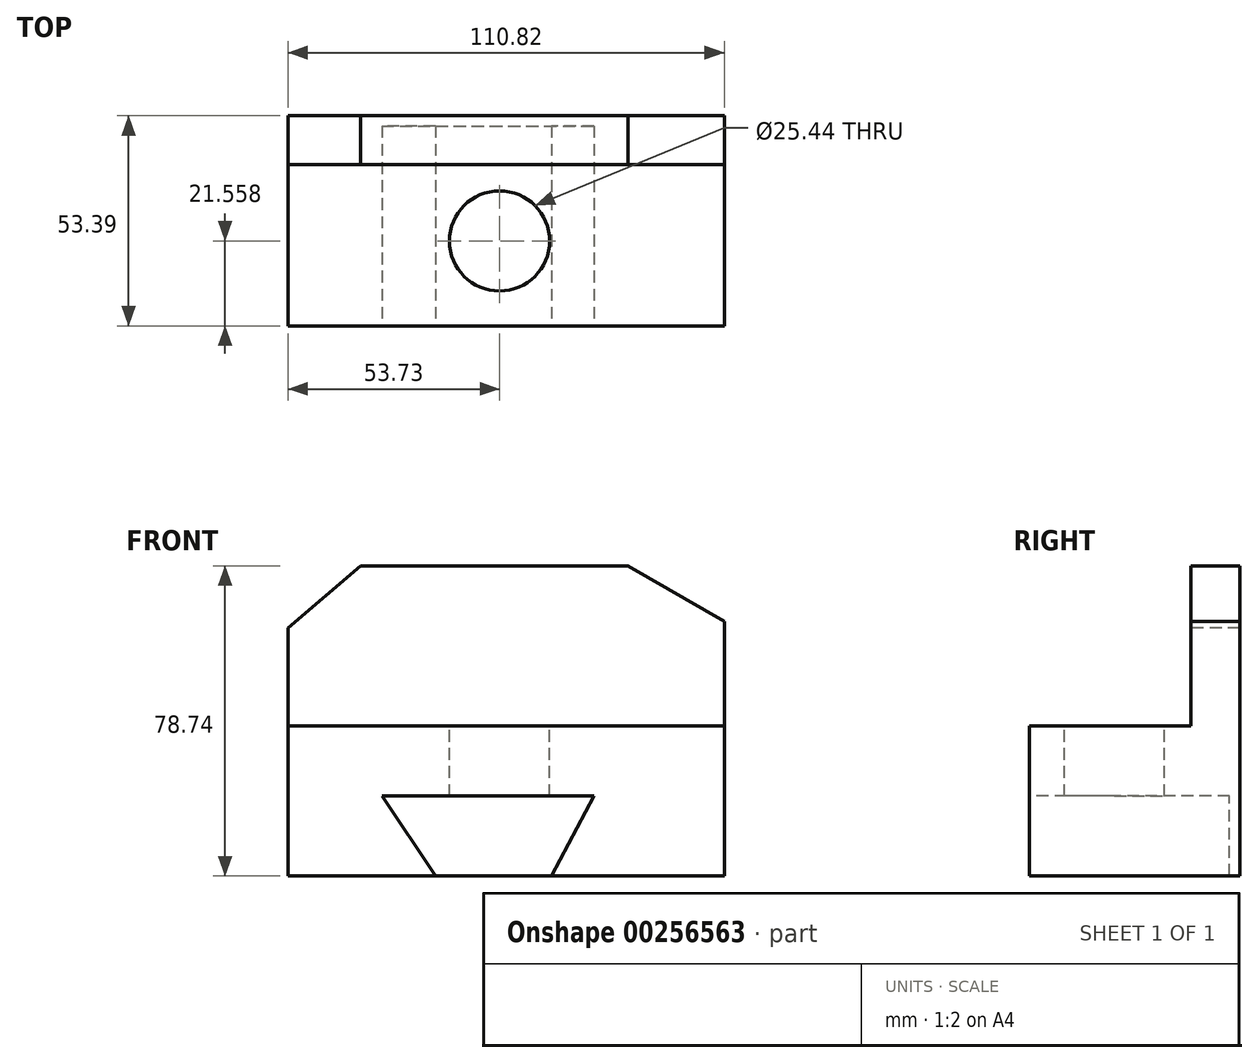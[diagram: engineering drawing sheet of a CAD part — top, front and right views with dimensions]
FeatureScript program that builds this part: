
annotation { "Feature Type Name" : "Feature", "Feature Type Description" : "" }
export const myFeature = defineFeature(function(context is Context, id is Id, definition is map)
    precondition{}
    {
        {
            var Q0;
            Q0=qCreatedBy(makeId("Top.planeOp"),FACE);
            var sketch = newSketch(context, id + "F0", { "sketchPlane" : qUnion([Q0])});
            skLineSegment(sketch, "E0.bottom", {"start": v(-53.73, 14.52) * mm, "end": v(57.1, 14.52) * mm});
            skLineSegment(sketch, "E0.top", {"start": v(-53.73, -38.87) * mm, "end": v(57.1, -38.87) * mm});
            skLineSegment(sketch, "E0.left", {"start": v(-53.73, 14.52) * mm, "end": v(-53.73, -38.87) * mm});
            skLineSegment(sketch, "E0.right", {"start": v(57.1, 14.52) * mm, "end": v(57.1, -38.87) * mm});
            skSolve(sketch);
        }
        {
            var Q0;
            Q0=makeQuery(id+"F0.imprint","IMPRINT",FACE,{"disambiguationData":[TD([[makeQuery(id+"F0.imprint","IMPRINT",EDGE,{"derivedFrom":sQuery(id+"F0.wireOp",EDGE,"E0.bottom")}),-1.0]])]});
            extrude(context, id + "F1", {"entities" : qUnion([Q0]), "depth" : 38.1 * mm});
        }
        {
            var Q0;
            Q0=makeQuery(id+"F1.opExtrude","CAP_FACE",FACE,{"disambiguationData":[OSD([sQuery(id+"F0.wireOp",EDGE,"E0.bottom"),sQuery(id+"F0.wireOp",EDGE,"E0.top"),sQuery(id+"F0.wireOp",EDGE,"E0.left"),sQuery(id+"F0.wireOp",EDGE,"E0.right")])],"isStart":false});
            var sketch = newSketch(context, id + "F2", { "sketchPlane" : qUnion([Q0])});
            skLineSegment(sketch, "E1.bottom", {"start": v(-53.73, 14.52) * mm, "end": v(57.1, 14.52) * mm});
            skLineSegment(sketch, "E1.top", {"start": v(-53.73, 2.1) * mm, "end": v(57.1, 2.1) * mm});
            skLineSegment(sketch, "E1.left", {"start": v(-53.73, 14.52) * mm, "end": v(-53.73, 2.1) * mm});
            skLineSegment(sketch, "E1.right", {"start": v(57.1, 14.52) * mm, "end": v(57.1, 2.1) * mm});
            skSolve(sketch);
        }
        {
            var Q0;
            Q0=makeQuery(id+"F2.imprint","IMPRINT",FACE,{"disambiguationData":[TD([[makeQuery(id+"F2.imprint","IMPRINT",EDGE,{"derivedFrom":sQuery(id+"F2.wireOp",EDGE,"E1.bottom")}),-1.0]])]});
            extrude(context, id + "F3", {"entities" : qUnion([Q0]), "operationType" : NewBodyOperationType.ADD, "depth" : 40.64 * mm});
        }
        {
            var Q0;
            Q0=makeQuery(id+"F3.opExtrude","SWEPT_FACE",FACE,{"disambiguationData":[OSD([sQuery(id+"F2.wireOp",EDGE,"E1.top")])]});
            var sketch = newSketch(context, id + "F4", { "sketchPlane" : qUnion([Q0])});
            skLineSegment(sketch, "E2", {"start": v(-35.27, 78.74) * mm, "end": v(-53.73, 63) * mm});
            skLineSegment(sketch, "E3", {"start": v(32.62, 78.74) * mm, "end": v(57.1, 64.6) * mm});
            skSolve(sketch);
        }
        {
            var Q0;
            {var subQ0=sQuery(id+"F4.wireOp",EDGE,"E2");Q0=makeQuery(id+"F4.imprint","IMPRINT",FACE,{"disambiguationData":[TD([[makeQuery(id+"F4.imprint","IMPRINT",EDGE,{"derivedFrom":subQ0}),-1.0]])]});}
            var Q1;
            {var subQ0=sQuery(id+"F4.wireOp",EDGE,"E3");Q1=makeQuery(id+"F4.imprint","IMPRINT",FACE,{"disambiguationData":[TD([[makeQuery(id+"F4.imprint","IMPRINT",EDGE,{"derivedFrom":subQ0}),1.0]])]});}
            extrude(context, id + "F5", {"entities" : qUnion([Q0, Q1]), "operationType" : NewBodyOperationType.REMOVE, "oppositeDirection" : true, "depth" : 25.4 * mm});
        }
        {
            var Q0;
            Q0=makeQuery(id+"F1.opExtrude","SWEPT_FACE",FACE,{"disambiguationData":[OSD([sQuery(id+"F0.wireOp",EDGE,"E0.top")])]});
            var sketch = newSketch(context, id + "F6", { "sketchPlane" : qUnion([Q0])});
            skLineSegment(sketch, "E4", {"start": v(-16.3, 0) * mm, "end": v(-29.88, 20.26) * mm});
            skLineSegment(sketch, "E5", {"start": v(-29.88, 20.26) * mm, "end": v(24.03, 20.26) * mm});
            skLineSegment(sketch, "E6", {"start": v(24.03, 20.26) * mm, "end": v(13.25, 0) * mm});
            skSolve(sketch);
        }
        {
            var Q0;
            {var subQ0=sQuery(id+"F6.wireOp",EDGE,"E4");Q0=makeQuery(id+"F6.imprint","IMPRINT",FACE,{"disambiguationData":[TD([[makeQuery(id+"F6.imprint","IMPRINT",EDGE,{"derivedFrom":subQ0}),-1.0]])]});}
            extrude(context, id + "F7", {"entities" : qUnion([Q0]), "operationType" : NewBodyOperationType.REMOVE, "oppositeDirection" : true, "depth" : 25.4 * mm});
        }
        {
            var Q0;
            Q0=makeQuery(id+"F7.boolean.opBoolean","COPY",FACE,{"derivedFrom":makeQuery(id+"F7.opExtrude","CAP_FACE",FACE,{"disambiguationData":[OSD([sQuery(id+"F0.wireOp",EDGE,"E0.top"),sQuery(id+"F6.wireOp",EDGE,"E4"),sQuery(id+"F6.wireOp",EDGE,"E5"),sQuery(id+"F6.wireOp",EDGE,"E6")])],"isStart":false})});
            extrude(context, id + "F8", {"entities" : qUnion([Q0]), "operationType" : NewBodyOperationType.REMOVE, "oppositeDirection" : true, "depth" : 25.4 * mm});
        }
        {
            var Q0;
            Q0=makeQuery(id+"F1.opExtrude","CAP_FACE",FACE,{"disambiguationData":[OSD([sQuery(id+"F0.wireOp",EDGE,"E0.bottom"),sQuery(id+"F0.wireOp",EDGE,"E0.top"),sQuery(id+"F0.wireOp",EDGE,"E0.left"),sQuery(id+"F0.wireOp",EDGE,"E0.right")])],"isStart":false});
            var sketch = newSketch(context, id + "F9", { "sketchPlane" : qUnion([Q0])});
            skLineSegment(sketch, "E7", {"start": v(0, -17.31) * mm, "end": v(0, -38.87) * mm});
            skLineSegment(sketch, "E8", {"start": v(0, -17.31) * mm, "end": v(-15.5, -17.31) * mm});
            skLineSegment(sketch, "E9", {"start": v(0, -17.31) * mm, "end": v(15.05, -17.31) * mm});
            skLineSegment(sketch, "E10", {"start": v(0, -17.31) * mm, "end": v(0, 0) * mm});
            skCircle(sketch, "E11", {"center": v(0, -17.31) * mm, "radius": 12.72 * mm});
            skSolve(sketch);
        }
        {
            var Q0;
            {var subQ1=sQuery(id+"F9.wireOp",EDGE,"E8");var subQ3=sQuery(id+"F9.wireOp",EDGE,"E11");var subQ4=makeQuery(id+"F9.imprint","INTERSECT",VERTEX,{"derivedFrom":[subQ1,subQ3]});Q0=makeQuery(id+"F9.imprint","IMPRINT",FACE,{"disambiguationData":[TD([[makeQuery(id+"F9.imprint","IMPRINT",EDGE,{"disambiguationData":[TD([[subQ4,1.0]])],"derivedFrom":subQ3}),1.0]])]});}
            var Q1;
            {var subQ1=sQuery(id+"F9.wireOp",EDGE,"E9");var subQ3=sQuery(id+"F9.wireOp",EDGE,"E11");var subQ4=makeQuery(id+"F9.imprint","INTERSECT",VERTEX,{"derivedFrom":[subQ1,subQ3]});Q1=makeQuery(id+"F9.imprint","IMPRINT",FACE,{"disambiguationData":[TD([[makeQuery(id+"F9.imprint","IMPRINT",EDGE,{"disambiguationData":[TD([[subQ4,-1.0]])],"derivedFrom":subQ3}),1.0]])]});}
            var Q2;
            {var subQ1=sQuery(id+"F9.wireOp",EDGE,"E7");var subQ3=sQuery(id+"F9.wireOp",EDGE,"E11");var subQ4=makeQuery(id+"F9.imprint","INTERSECT",VERTEX,{"derivedFrom":[subQ1,subQ3]});Q2=makeQuery(id+"F9.imprint","IMPRINT",FACE,{"disambiguationData":[TD([[makeQuery(id+"F9.imprint","IMPRINT",EDGE,{"disambiguationData":[TD([[subQ4,1.0]])],"derivedFrom":subQ3}),1.0]])]});}
            var Q3;
            {var subQ1=sQuery(id+"F9.wireOp",EDGE,"E7");var subQ3=sQuery(id+"F9.wireOp",EDGE,"E11");var subQ4=makeQuery(id+"F9.imprint","INTERSECT",VERTEX,{"derivedFrom":[subQ1,subQ3]});Q3=makeQuery(id+"F9.imprint","IMPRINT",FACE,{"disambiguationData":[TD([[makeQuery(id+"F9.imprint","IMPRINT",EDGE,{"disambiguationData":[TD([[subQ4,-1.0]])],"derivedFrom":subQ3}),1.0]])]});}
            extrude(context, id + "F10", {"entities" : qUnion([Q0, Q1, Q2, Q3]), "operationType" : NewBodyOperationType.REMOVE, "oppositeDirection" : true, "depth" : 25.4 * mm});
        }
    });
